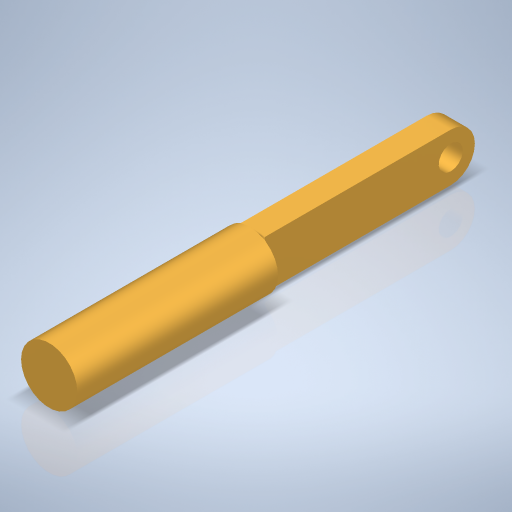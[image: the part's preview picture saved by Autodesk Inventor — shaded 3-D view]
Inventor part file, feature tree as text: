
AUTODESK INVENTOR PART (.ipt)
format: ipt  version: 2024 (Build 280153000, 153)  size: 301,568 bytes
history: native  units: mm
features: sketch x3, extrude x2, plane x1, fillet x1, hole x1, projected_geometry x1
ambient origin geometry x8: Origin, YZ Plane, XZ Plane, XY Plane, X Axis, Y Axis, Z Axis, Center Point
bodies: Body1 (feature_tree)
feature tree (9):
  extrude  "Extrusion5"  Depth=25.0mm TaperAngle=0.0deg
  plane  "Arbeitsebene1"
  extrude  "Extrusion6"  Depth=3.0mm TaperAngle=0.0deg
  fillet  "Rundung1"  Radius=3.0mm
  hole  "Bohrung1"  [1 undecoded]
  sketch  "Skizze7"  dims[d13=7.0mm d14=25.0mm d15=0.0mm]
  sketch  "Skizze9"  dims[d16=0.0mm d18=3.0mm d19=0.0mm d20=3.0mm]
  projected_geometry  "Projizierte Kontur1"
  sketch  "Skizze10"  dims[d21=23.5mm d22=6.0mm d23=0.5mm d24=3.0mm d25=6.0mm d26=4.0mm d27=2.0mm d28=90.0deg d29=4.0mm d30=0.0mm]
note: 1 required parameter value undecoded (feature->parameter linkage not recoverable at this tier; creation-order binding heuristic only, values carry confidence <= 0.55)
